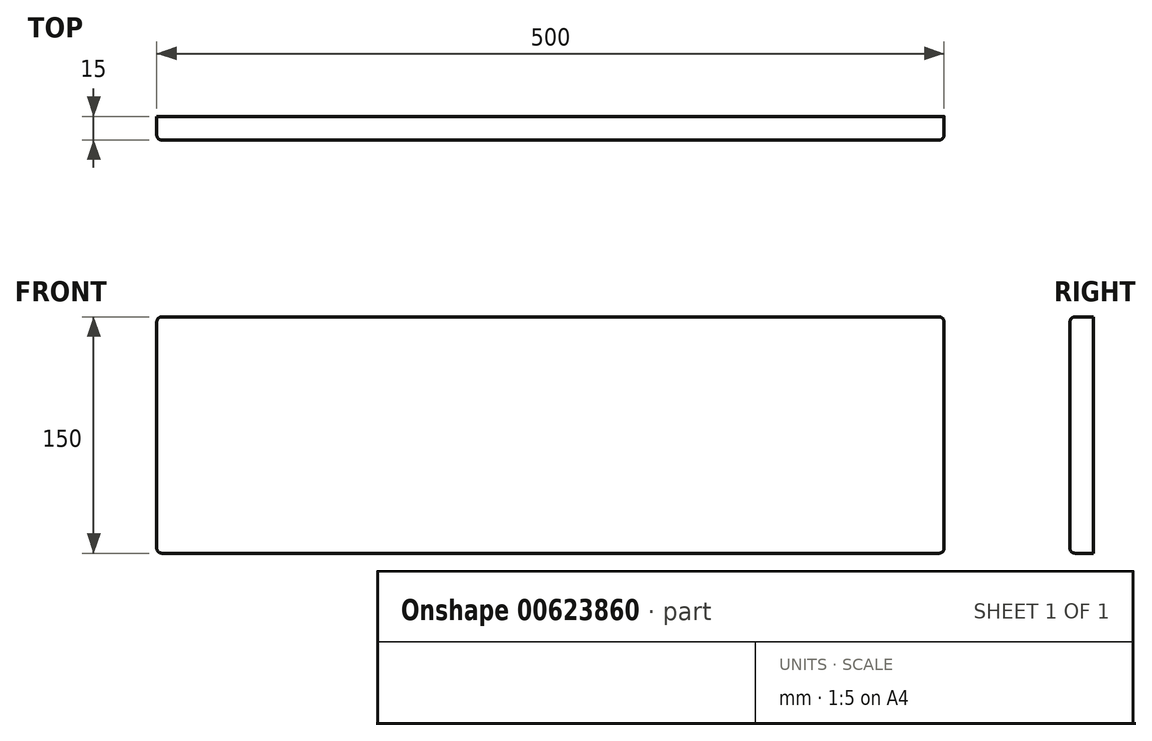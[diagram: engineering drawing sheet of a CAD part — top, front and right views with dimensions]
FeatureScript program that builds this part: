
annotation { "Feature Type Name" : "Feature", "Feature Type Description" : "" }
export const myFeature = defineFeature(function(context is Context, id is Id, definition is map)
    precondition{}
    {
        {
            var Q0;
            Q0=qCreatedBy(makeId("Front.planeOp"),FACE);
            var sketch = newSketch(context, id + "F0", { "sketchPlane" : qUnion([Q0])});
            skLineSegment(sketch, "E0.bottom", {"start": v(0, 0) * mm, "end": v(500, 0) * mm});
            skLineSegment(sketch, "E0.top", {"start": v(0, 150) * mm, "end": v(500, 150) * mm});
            skLineSegment(sketch, "E0.left", {"start": v(0, 150) * mm, "end": v(0, 0) * mm});
            skLineSegment(sketch, "E0.right", {"start": v(500, 150) * mm, "end": v(500, 0) * mm});
            skSolve(sketch);
        }
        {
            var Q0;
            Q0 = qSketchRegion(id + "F0", true);
            extrude(context, id + "F1", {"entities" : qUnion([Q0]), "depth" : 15 * mm, "offsetDistance" : 25 * mm});
        }
        {
            var Q0;
            Q0=makeQuery(id+"F1.opExtrude","CAP_EDGE",EDGE,{"disambiguationData":[OSD([sQuery(id+"F0.wireOp",EDGE,"E0.top")])],"isStart":false});
            var Q1;
            Q1=makeQuery(id+"F1.opExtrude","CAP_EDGE",EDGE,{"disambiguationData":[OSD([sQuery(id+"F0.wireOp",EDGE,"E0.bottom")])],"isStart":false});
            var Q2;
            Q2=makeQuery(id+"F1.opExtrude","CAP_EDGE",EDGE,{"disambiguationData":[OSD([sQuery(id+"F0.wireOp",EDGE,"E0.left")])],"isStart":false});
            var Q3;
            Q3=makeQuery(id+"F1.opExtrude","CAP_EDGE",EDGE,{"disambiguationData":[OSD([sQuery(id+"F0.wireOp",EDGE,"E0.right")])],"isStart":false});
            var Q4;
            Q4=makeQuery(id+"F1.opExtrude","SWEPT_EDGE",EDGE,{"disambiguationData":[OSD([sQuery(id+"F0.wireOp",EDGE,"E0.top"),sQuery(id+"F0.wireOp",EDGE,"E0.left")])]});
            var Q5;
            Q5=makeQuery(id+"F1.opExtrude","SWEPT_EDGE",EDGE,{"disambiguationData":[OSD([sQuery(id+"F0.wireOp",EDGE,"E0.bottom"),sQuery(id+"F0.wireOp",EDGE,"E0.left")])]});
            var Q6;
            Q6=makeQuery(id+"F1.opExtrude","SWEPT_EDGE",EDGE,{"disambiguationData":[OSD([sQuery(id+"F0.wireOp",EDGE,"E0.bottom"),sQuery(id+"F0.wireOp",EDGE,"E0.right")])]});
            var Q7;
            Q7=makeQuery(id+"F1.opExtrude","SWEPT_EDGE",EDGE,{"disambiguationData":[OSD([sQuery(id+"F0.wireOp",EDGE,"E0.top"),sQuery(id+"F0.wireOp",EDGE,"E0.right")])]});
            fillet(context, id + "F2", {"entities" : qUnion([Q0, Q1, Q2, Q3, Q4, Q5, Q6, Q7]), "radius" : 3 * mm, "tangentPropagation" : true, "allowEdgeOverflow" : false});
        }
    });
